# Revit family: 290170 OvaLED R Round S NM ST LED 230V 1t Tak
name_source: partatom
category: Lighting Fixtures
revit_build: Autodesk Revit 2016 (Build: 20160314_0715(x64)
units: mm (PartAtom-declared; Revit-internal decimal feet)

## family parameters
Always vertical = Yes
Cut with Voids When Loaded = No
Light Source = Yes
OmniClass Number = 23.80.70.11.21
OmniClass Title = Emergency Lighting
Part Type = Normal
Room Calculation Point = No
Round Connector Dimension = Use Diameter
Shared = No
Work Plane-Based = No

## types (2) — shared parameters
Batteri bredde = 40 mm
Batteri høyde = 20 mm  [stored 0.0656168 ft]
Batteri lengde = 300 mm
Color Filter = 16777215
Diameter = 102 mm  [stored 0.334646 ft]
Dimming Lamp Color Temperature Shift = <None>
Emit Shape Visible in Rendering = No
Emit from Circle Diameter = 102 mm  [stored 0.334646 ft]
Glass Material = Plastic - Transparent
Height = 4 mm  [stored 0.0131234 ft]
Kabellengde = 220 mm
Material = Plastic - White
Number of Poles = 1
Photometric Web File = 2x4 3Lamp.ies
Tilt Angle = 90.00°
Voltage = 230 V

## per-type parameters (varying)
| type | Assembly Code | Batteri | Keynote | Manufacturer | NS8360 | Type Comments |
| Med batteri | 4432 | Yes | WT2 | Honeywell | 4432_WT2 | -UN |
| Uten Batteri |  | No |  |  |  |  |

note: [stored X ft] marks values corroborated as IEEE doubles in the binary element streams (Revit-internal decimal feet)

## geometry (parser evidence)
native form markers: Sweep x5
no freeform markers — native parametric forms only
